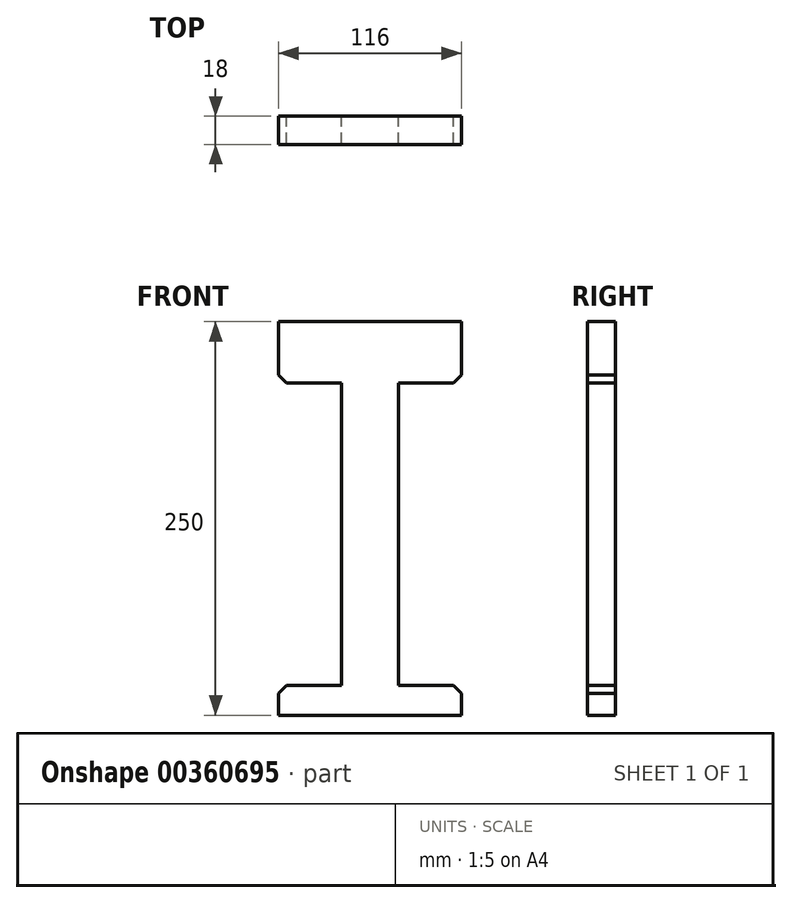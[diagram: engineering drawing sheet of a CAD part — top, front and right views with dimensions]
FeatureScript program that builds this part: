
annotation { "Feature Type Name" : "Feature", "Feature Type Description" : "" }
export const myFeature = defineFeature(function(context is Context, id is Id, definition is map)
    precondition{}
    {
        {
            var Q0;
            Q0=qCreatedBy(makeId("Front.planeOp"),FACE);
            var sketch = newSketch(context, id + "F0", { "sketchPlane" : qUnion([Q0])});
            skLineSegment(sketch, "E0.bottom", {"start": v(0, 0) * mm, "end": v(116, 0) * mm});
            skLineSegment(sketch, "E0.top", {"start": v(0, 19) * mm, "end": v(40, 19) * mm});
            skLineSegment(sketch, "E0.left", {"start": v(0, 0) * mm, "end": v(0, 19) * mm});
            skLineSegment(sketch, "E1.bottom", {"start": v(0, 211) * mm, "end": v(40, 211) * mm});
            skLineSegment(sketch, "E1.top", {"start": v(0, 250) * mm, "end": v(116, 250) * mm});
            skLineSegment(sketch, "E1.left", {"start": v(0, 211) * mm, "end": v(0, 250) * mm});
            skLineSegment(sketch, "E2", {"start": v(40, 211) * mm, "end": v(40, 19) * mm});
            skLineSegment(sketch, "E3", {"start": v(116, 250) * mm, "end": v(116, 211) * mm});
            skLineSegment(sketch, "E4.bottom", {"start": v(116, 211) * mm, "end": v(76, 211) * mm});
            skLineSegment(sketch, "E4.top", {"start": v(116, 19) * mm, "end": v(76, 19) * mm});
            skLineSegment(sketch, "E4.right", {"start": v(76, 211) * mm, "end": v(76, 19) * mm});
            skLineSegment(sketch, "E5.trimOffspring", {"start": v(116, 19) * mm, "end": v(116, 0) * mm});
            skSolve(sketch);
        }
        {
            var Q0;
            Q0=makeQuery(id+"F0.imprint","IMPRINT",FACE,{"disambiguationData":[TD([[makeQuery(id+"F0.imprint","IMPRINT",EDGE,{"derivedFrom":sQuery(id+"F0.wireOp",EDGE,"E0.bottom")}),1.0]])]});
            extrude(context, id + "F1", {"entities" : qUnion([Q0]), "depth" : 18 * mm});
        }
        {
            var Q0;
            Q0=makeQuery(id+"F1.opExtrude","SWEPT_EDGE",EDGE,{"disambiguationData":[OSD([sQuery(id+"F0.wireOp",EDGE,"E1.bottom"),sQuery(id+"F0.wireOp",EDGE,"E1.left")])]});
            var Q1;
            Q1=makeQuery(id+"F1.opExtrude","SWEPT_EDGE",EDGE,{"disambiguationData":[OSD([sQuery(id+"F0.wireOp",EDGE,"E0.top"),sQuery(id+"F0.wireOp",EDGE,"E0.left")])]});
            var Q2;
            Q2=makeQuery(id+"F1.opExtrude","SWEPT_EDGE",EDGE,{"disambiguationData":[OSD([sQuery(id+"F0.wireOp",EDGE,"E4.top"),sQuery(id+"F0.wireOp",EDGE,"E5.trimOffspring")])]});
            var Q3;
            Q3=makeQuery(id+"F1.opExtrude","SWEPT_EDGE",EDGE,{"disambiguationData":[OSD([sQuery(id+"F0.wireOp",EDGE,"E3"),sQuery(id+"F0.wireOp",EDGE,"E4.bottom")])]});
            chamfer(context, id + "F2", {"entities" : qUnion([Q0, Q1, Q2, Q3]), "width" : 5 * mm, "tangentPropagation" : true});
        }
    });
